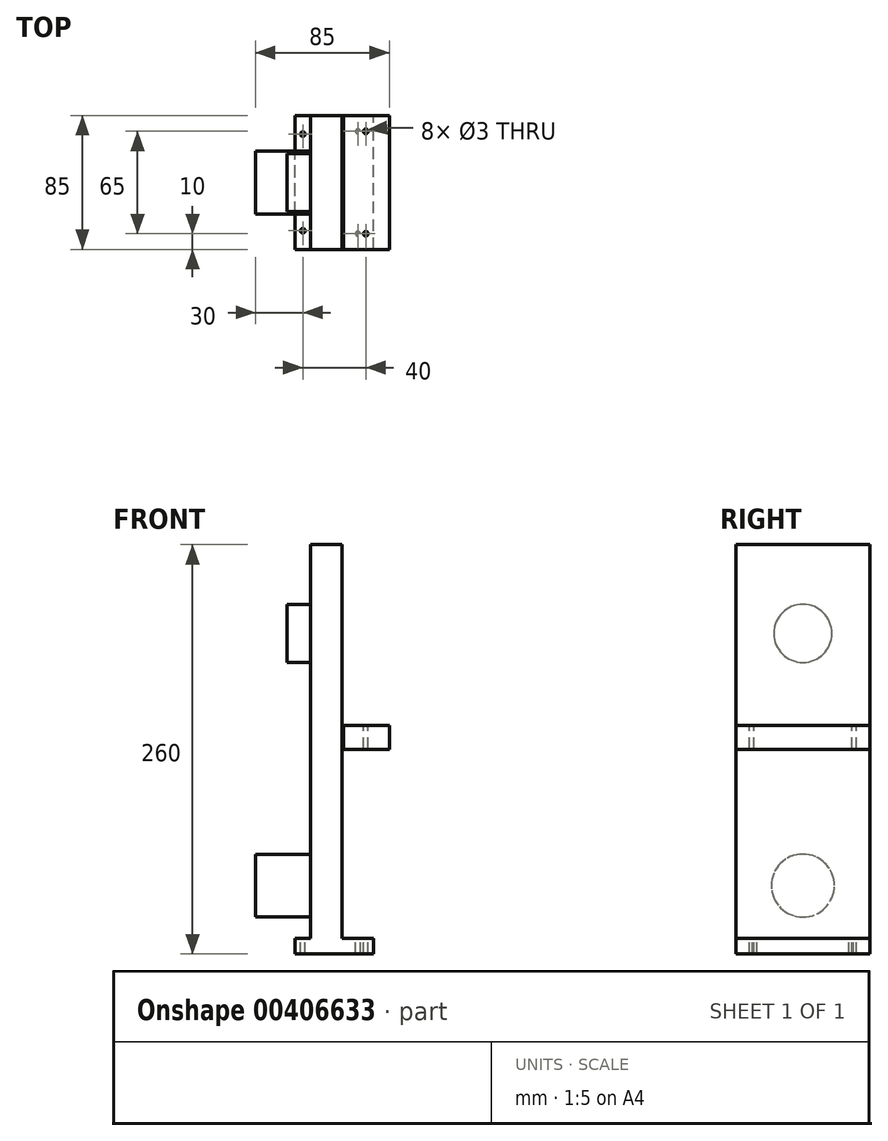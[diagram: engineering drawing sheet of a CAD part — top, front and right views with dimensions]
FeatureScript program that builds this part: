
annotation { "Feature Type Name" : "Feature", "Feature Type Description" : "" }
export const myFeature = defineFeature(function(context is Context, id is Id, definition is map)
    precondition{}
    {
        {
            var Q0;
            Q0=qCreatedBy(makeId("Top.planeOp"),FACE);
            var sketch = newSketch(context, id + "F0", { "sketchPlane" : qUnion([Q0])});
            skLineSegment(sketch, "E0.bottom", {"start": v(25, -42.5) * mm, "end": v(-25, -42.5) * mm});
            skLineSegment(sketch, "E0.top", {"start": v(25, 42.5) * mm, "end": v(-25, 42.5) * mm});
            skLineSegment(sketch, "E0.left", {"start": v(25, -42.5) * mm, "end": v(25, 42.5) * mm});
            skLineSegment(sketch, "E0.right", {"start": v(-25, -42.5) * mm, "end": v(-25, 42.5) * mm});
            skPoint(sketch, "E0.middle", {"position": v(0, 0) * mm});
            skSolve(sketch);
        }
        {
            var Q0;
            Q0 = qSketchRegion(id + "F0", true);
            extrude(context, id + "F1", {"entities" : qUnion([Q0]), "depth" : 10 * mm});
        }
        {
            var Q0;
            Q0=makeQuery(id+"F1.opExtrude","CAP_FACE",FACE,{"disambiguationData":[OSD([sQuery(id+"F0.wireOp",EDGE,"E0.bottom"),sQuery(id+"F0.wireOp",EDGE,"E0.top"),sQuery(id+"F0.wireOp",EDGE,"E0.left"),sQuery(id+"F0.wireOp",EDGE,"E0.right")])],"isStart":false});
            var sketch = newSketch(context, id + "F2", { "sketchPlane" : qUnion([Q0])});
            skLineSegment(sketch, "E1.bottom", {"start": v(-25, 42.5) * mm, "end": v(5, 42.5) * mm});
            skLineSegment(sketch, "E1.top", {"start": v(-15, -42.5) * mm, "end": v(5, -42.5) * mm});
            skLineSegment(sketch, "E1.left", {"start": v(-15, 42.5) * mm, "end": v(-15, -42.5) * mm});
            skLineSegment(sketch, "E1.right", {"start": v(5, 42.5) * mm, "end": v(5, -42.5) * mm});
            skSolve(sketch);
        }
        {
            var Q0;
            Q0=makeQuery(id+"F2.imprint","IMPRINT",FACE,{"disambiguationData":[TD([[makeQuery(id+"F2.imprint","IMPRINT",EDGE,{"derivedFrom":sQuery(id+"F2.wireOp",EDGE,"E1.top")}),-1.0]])]});
            extrude(context, id + "F3", {"entities" : qUnion([Q0]), "operationType" : NewBodyOperationType.ADD, "depth" : 250 * mm});
        }
        {
            var Q0;
            Q0=makeQuery(id+"F3.opExtrude","SWEPT_FACE",FACE,{"disambiguationData":[OSD([sQuery(id+"F2.wireOp",EDGE,"E1.right")])]});
            var sketch = newSketch(context, id + "F4", { "sketchPlane" : qUnion([Q0])});
            skLineSegment(sketch, "E2.bottom", {"start": v(-42.5, 145) * mm, "end": v(42.5, 145) * mm});
            skLineSegment(sketch, "E2.top", {"start": v(-42.5, 130) * mm, "end": v(42.5, 130) * mm});
            skLineSegment(sketch, "E2.left", {"start": v(-42.5, 145) * mm, "end": v(-42.5, 130) * mm});
            skLineSegment(sketch, "E2.right", {"start": v(42.5, 145) * mm, "end": v(42.5, 130) * mm});
            skSolve(sketch);
        }
        {
            var Q0;
            Q0 = qSketchRegion(id + "F4", true);
            extrude(context, id + "F5", {"entities" : qUnion([Q0]), "operationType" : NewBodyOperationType.ADD, "depth" : 30 * mm});
        }
        {
            var Q0;
            {var subQ0=sQuery(id+"F0.wireOp",EDGE,"E0.top");var subQ1=sQuery(id+"F0.wireOp",EDGE,"E0.right");var subQ2=sQuery(id+"F0.wireOp",EDGE,"E0.bottom");Q0=makeQuery(id+"F3.boolean.opBoolean","SPLIT",FACE,{"disambiguationData":[TD([makeQuery(id+"F1.opExtrude","SWEPT_FACE",FACE,{"disambiguationData":[OSD([subQ1])]})])],"derivedFrom":makeQuery(id+"F1.opExtrude","CAP_FACE",FACE,{"disambiguationData":[OSD([subQ2,subQ0,sQuery(id+"F0.wireOp",EDGE,"E0.left"),subQ1])],"isStart":false})});}
            var sketch = newSketch(context, id + "F6", { "sketchPlane" : qUnion([Q0])});
            skLineSegment(sketch, "E3", {"start": v(-20, 42.5) * mm, "end": v(-20, -42.5) * mm, "construction": true});
            skPoint(sketch, "E4", {"position": v(-20, 30.76) * mm});
            skPoint(sketch, "E5", {"position": v(-20, -30.66) * mm});
            skSolve(sketch);
        }
        {
            var Q0;
            Q0=makeQuery(id+"F5.opExtrude","SWEPT_FACE",FACE,{"disambiguationData":[OSD([sQuery(id+"F4.wireOp",EDGE,"E2.bottom")])]});
            var sketch = newSketch(context, id + "F7", { "sketchPlane" : qUnion([Q0])});
            skLineSegment(sketch, "E6", {"start": v(20, 42.5) * mm, "end": v(20, -42.5) * mm, "construction": true});
            skPoint(sketch, "E7", {"position": v(20, 32.5) * mm});
            skPoint(sketch, "E8", {"position": v(20, -32.5) * mm});
            skSolve(sketch);
        }
        {
            var Q0;
            {var subQ0=sQuery(id+"F0.wireOp",EDGE,"E0.left");var subQ1=sQuery(id+"F0.wireOp",EDGE,"E0.top");var subQ2=sQuery(id+"F0.wireOp",EDGE,"E0.bottom");Q0=makeQuery(id+"F3.boolean.opBoolean","SPLIT",FACE,{"disambiguationData":[TD([makeQuery(id+"F1.opExtrude","SWEPT_FACE",FACE,{"disambiguationData":[OSD([subQ0])]})])],"derivedFrom":makeQuery(id+"F1.opExtrude","CAP_FACE",FACE,{"disambiguationData":[OSD([subQ2,subQ1,subQ0,sQuery(id+"F0.wireOp",EDGE,"E0.right")])],"isStart":false})});}
            var sketch = newSketch(context, id + "F8", { "sketchPlane" : qUnion([Q0])});
            skLineSegment(sketch, "E9", {"start": v(15, -42.5) * mm, "end": v(15, 42.5) * mm, "construction": true});
            skPoint(sketch, "E10", {"position": v(15, 32.5) * mm});
            skPoint(sketch, "E11", {"position": v(15, -32.5) * mm});
            skSolve(sketch);
        }
        {
            var Q0;
            Q0=sQuery(id+"F7.wireOp",VERTEX,"E7");
            var Q1;
            Q1=sQuery(id+"F7.wireOp",VERTEX,"E8");
            var Q2;
            Q2=sQuery(id+"F6.wireOp",VERTEX,"E4");
            var Q3;
            Q3=sQuery(id+"F6.wireOp",VERTEX,"E5");
            var Q4;
            Q4=sQuery(id+"F8.wireOp",VERTEX,"E11");
            var Q5;
            Q5=sQuery(id+"F8.wireOp",VERTEX,"E10");
            var Q6;
            Q6=makeQuery(id+"F1.opExtrude","SWEPT_BODY",BODY,{"disambiguationData":[OSD([sQuery(id+"F0.wireOp",EDGE,"E0.bottom"),sQuery(id+"F0.wireOp",EDGE,"E0.top"),sQuery(id+"F0.wireOp",EDGE,"E0.left"),sQuery(id+"F0.wireOp",EDGE,"E0.right")])]});
            hole(context, id + "F9", {"style" : HoleStyle.SIMPLE, "endStyle" : HoleEndStyle.THROUGH, "holeDiameter" : 3 * mm, "isTappedThrough" : true, "tappedDepth" : 12 * mm, "tapClearance" : 3, "startFromSketch" : true, "locations" : qUnion([Q0, Q1, Q2, Q3, Q4, Q5]), "scope" : qUnion([Q6])});
        }
        {
            var Q0;
            Q0=makeQuery(id+"F3.opExtrude","SWEPT_FACE",FACE,{"disambiguationData":[OSD([sQuery(id+"F2.wireOp",EDGE,"E1.left")])]});
            var sketch = newSketch(context, id + "F10", { "sketchPlane" : qUnion([Q0])});
            skCircle(sketch, "E12", {"center": v(0, 43.38) * mm, "radius": 20 * mm});
            skSolve(sketch);
        }
        {
            var Q0;
            Q0 = qSketchRegion(id + "F10", true);
            extrude(context, id + "F11", {"entities" : qUnion([Q0]), "operationType" : NewBodyOperationType.ADD, "depth" : 35 * mm});
        }
        {
            var Q0;
            Q0=makeQuery(id+"F3.opExtrude","SWEPT_FACE",FACE,{"disambiguationData":[OSD([sQuery(id+"F2.wireOp",EDGE,"E1.left")])]});
            var sketch = newSketch(context, id + "F12", { "sketchPlane" : qUnion([Q0])});
            skCircle(sketch, "E13", {"center": v(0, 203.59) * mm, "radius": 18.48 * mm});
            skSolve(sketch);
        }
        {
            var Q0;
            Q0 = qSketchRegion(id + "F12", true);
            extrude(context, id + "F13", {"entities" : qUnion([Q0]), "operationType" : NewBodyOperationType.ADD, "depth" : 15 * mm});
        }
        {
            var Q0;
            Q0=makeQuery(id+"F5.boolean.opBoolean","MERGE",FACE,{"derivedFrom":[makeQuery(id+"F3.boolean.opBoolean","MERGE",FACE,{"derivedFrom":[makeQuery(id+"F1.opExtrude","SWEPT_FACE",FACE,{"disambiguationData":[OSD([sQuery(id+"F0.wireOp",EDGE,"E0.bottom")])]}),makeQuery(id+"F3.opExtrude","SWEPT_FACE",FACE,{"disambiguationData":[OSD([sQuery(id+"F2.wireOp",EDGE,"E1.top")])]})]}),makeQuery(id+"F5.opExtrude","SWEPT_FACE",FACE,{"disambiguationData":[OSD([sQuery(id+"F4.wireOp",EDGE,"E2.left")])]})]});
            var sketch = newSketch(context, id + "F14", { "sketchPlane" : qUnion([Q0])});
            skLineSegment(sketch, "E14.bottom", {"start": v(5, 145) * mm, "end": v(6, 145) * mm});
            skLineSegment(sketch, "E14.top", {"start": v(5, 130) * mm, "end": v(6, 130) * mm});
            skLineSegment(sketch, "E14.left", {"start": v(5, 145) * mm, "end": v(5, 130) * mm});
            skLineSegment(sketch, "E14.right", {"start": v(6, 145) * mm, "end": v(6, 130) * mm});
            skSolve(sketch);
        }
        {
            var Q0;
            Q0=makeQuery(id+"F14.imprint","IMPRINT",FACE,{"disambiguationData":[TD([[makeQuery(id+"F14.imprint","IMPRINT",EDGE,{"derivedFrom":sQuery(id+"F14.wireOp",EDGE,"E14.bottom")}),1.0]])]});
            var Q1;
            Q1=makeQuery(id+"F5.boolean.opBoolean","MERGE",FACE,{"derivedFrom":[makeQuery(id+"F3.boolean.opBoolean","MERGE",FACE,{"derivedFrom":[makeQuery(id+"F1.opExtrude","SWEPT_FACE",FACE,{"disambiguationData":[OSD([sQuery(id+"F0.wireOp",EDGE,"E0.top")])]}),makeQuery(id+"F3.opExtrude","SWEPT_FACE",FACE,{"disambiguationData":[OSD([sQuery(id+"F2.wireOp",EDGE,"E1.bottom")])]})]}),makeQuery(id+"F5.opExtrude","SWEPT_FACE",FACE,{"disambiguationData":[OSD([sQuery(id+"F4.wireOp",EDGE,"E2.right")])]})]});
            extrude(context, id + "F15", {"entities" : qUnion([Q0]), "operationType" : NewBodyOperationType.REMOVE, "endBound" : BoundingType.UP_TO_SURFACE, "oppositeDirection" : true, "endBoundEntityFace" : qUnion([Q1]), "depth" : 25 * mm});
        }
    });
